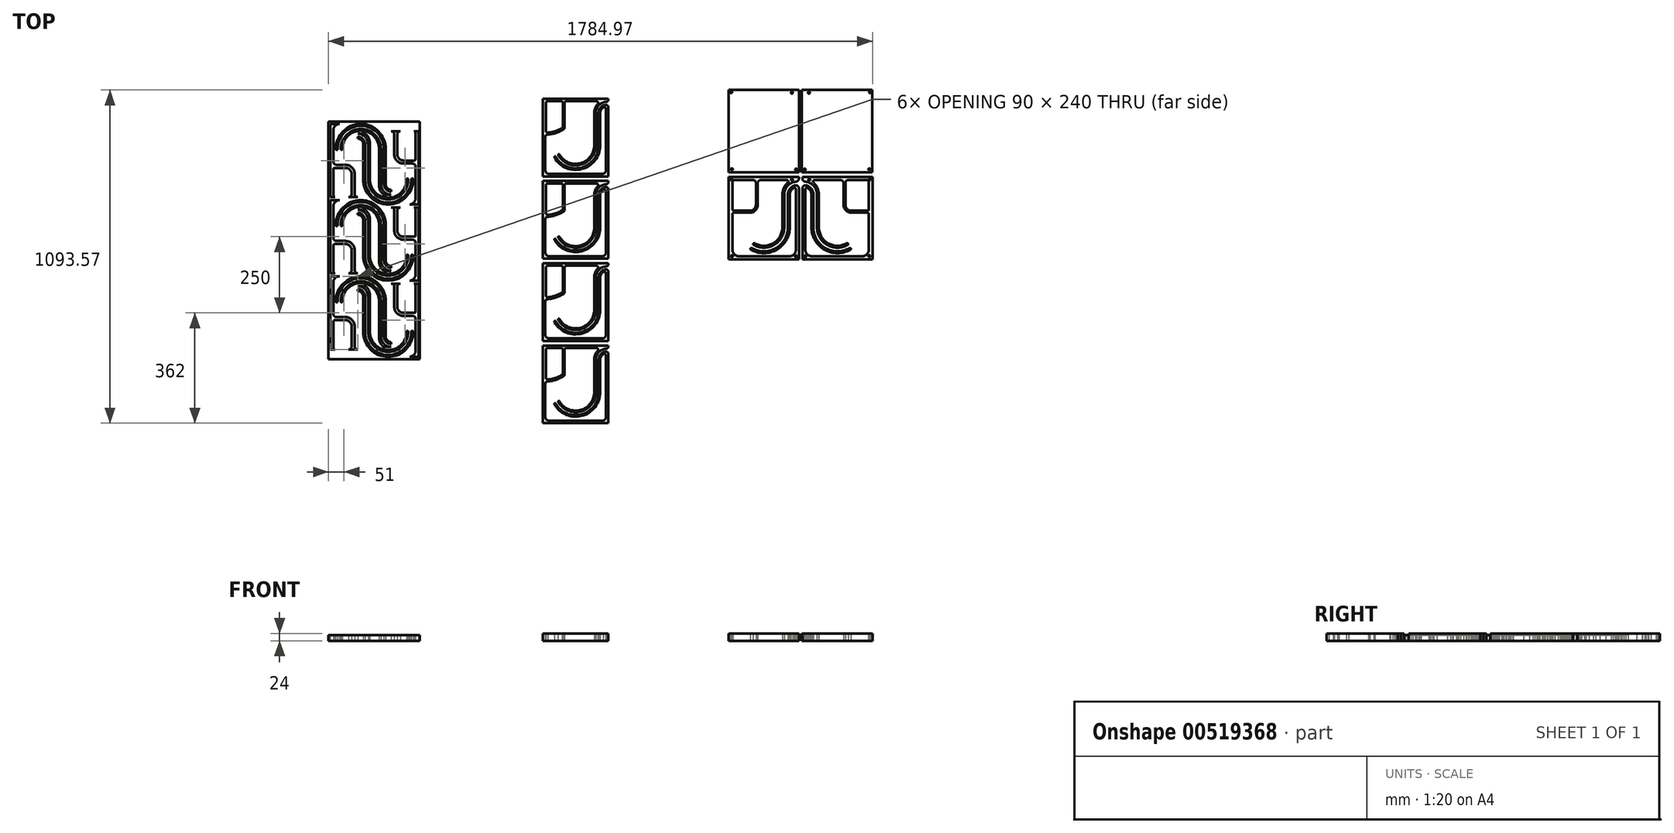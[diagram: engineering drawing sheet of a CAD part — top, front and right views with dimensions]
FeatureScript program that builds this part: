
annotation { "Feature Type Name" : "Feature", "Feature Type Description" : "" }
export const myFeature = defineFeature(function(context is Context, id is Id, definition is map)
    precondition{}
    {
        {
            var Q0;
            Q0=qCreatedBy(makeId("Top.planeOp"),FACE);
            var sketch = newSketch(context, id + "F0", { "sketchPlane" : qUnion([Q0])});
            skLineSegment(sketch, "E0", {"start": v(-576, 116) * mm, "end": v(-576, 0) * mm});
            skArc(sketch, "E1", {"start": v(-560, 116) * mm, "mid": v(-563.31, 134.85) * mm, "end": v(-575, 150) * mm});
            skArc(sketch, "E2", {"start": v(-582, 116) * mm, "mid": v(-587.27, 128.73) * mm, "end": v(-600, 134) * mm});
            skLineSegment(sketch, "E3", {"start": v(-600, 134) * mm, "end": v(-600, 140) * mm});
            skArc(sketch, "E4", {"start": v(-576, 116) * mm, "mid": v(-583.03, 132.97) * mm, "end": v(-600, 140) * mm});
            skArc(sketch, "E5", {"start": v(-566, 116) * mm, "mid": v(-575.96, 140.04) * mm, "end": v(-600, 150) * mm});
            skLineSegment(sketch, "E6", {"start": v(-582, 116) * mm, "end": v(-582, 0) * mm});
            skArc(sketch, "E7", {"start": v(-560, 0) * mm, "mid": v(-500, -60) * mm, "end": v(-440, 0) * mm});
            skLineSegment(sketch, "E8", {"start": v(-560, 116) * mm, "end": v(-560, 0) * mm});
            skArc(sketch, "E9", {"start": v(-566, 0) * mm, "mid": v(-500, -66) * mm, "end": v(-434, 0) * mm});
            skArc(sketch, "E10", {"start": v(-576, 0) * mm, "mid": v(-500, -76) * mm, "end": v(-424, 0) * mm});
            skArc(sketch, "E11", {"start": v(-582, 0) * mm, "mid": v(-500, -82) * mm, "end": v(-418, 0) * mm});
            skArc(sketch, "E12", {"start": v(-434, 0) * mm, "mid": v(-437, 3) * mm, "end": v(-440, 0) * mm});
            skArc(sketch, "E13", {"start": v(-418, 0) * mm, "mid": v(-421, 3) * mm, "end": v(-424, 0) * mm});
            skLineSegment(sketch, "E14", {"start": v(-600, 150) * mm, "end": v(-575, 150) * mm});
            skLineSegment(sketch, "E15", {"start": v(-566, 116) * mm, "end": v(-566, 0) * mm});
            skLineSegment(sketch, "E16", {"start": v(-514, -16) * mm, "end": v(-514, 100) * mm});
            skArc(sketch, "E17", {"start": v(-530, -16) * mm, "mid": v(-526.69, -34.85) * mm, "end": v(-515, -50) * mm});
            skArc(sketch, "E18", {"start": v(-508, -16) * mm, "mid": v(-502.73, -28.73) * mm, "end": v(-490, -34) * mm});
            skLineSegment(sketch, "E19", {"start": v(-490, -34) * mm, "end": v(-490, -40) * mm});
            skArc(sketch, "E20", {"start": v(-514, -16) * mm, "mid": v(-506.97, -32.97) * mm, "end": v(-490, -40) * mm});
            skArc(sketch, "E21", {"start": v(-524, -16) * mm, "mid": v(-514.04, -40.04) * mm, "end": v(-490, -50) * mm});
            skLineSegment(sketch, "E22", {"start": v(-508, -16) * mm, "end": v(-508, 100) * mm});
            skArc(sketch, "E23", {"start": v(-530, 100) * mm, "mid": v(-590, 160) * mm, "end": v(-650, 100) * mm});
            skLineSegment(sketch, "E24", {"start": v(-530, -16) * mm, "end": v(-530, 100) * mm});
            skArc(sketch, "E25", {"start": v(-524, 100) * mm, "mid": v(-590, 166) * mm, "end": v(-656, 100) * mm});
            skArc(sketch, "E26", {"start": v(-514, 100) * mm, "mid": v(-590, 176) * mm, "end": v(-666, 100) * mm});
            skArc(sketch, "E27", {"start": v(-508, 100) * mm, "mid": v(-590, 182) * mm, "end": v(-672, 100) * mm});
            skArc(sketch, "E28", {"start": v(-656, 100) * mm, "mid": v(-653, 97) * mm, "end": v(-650, 100) * mm});
            skArc(sketch, "E29", {"start": v(-672, 100) * mm, "mid": v(-669, 97) * mm, "end": v(-666, 100) * mm});
            skLineSegment(sketch, "E30", {"start": v(-490, -50) * mm, "end": v(-515, -50) * mm});
            skLineSegment(sketch, "E31", {"start": v(-524, -16) * mm, "end": v(-524, 100) * mm});
            skArc(sketch, "E32", {"start": v(-430, -82) * mm, "mid": v(-415.86, -76.14) * mm, "end": v(-410, -62) * mm});
            skArc(sketch, "E33", {"start": v(-410, 42) * mm, "mid": v(-412.93, 49.07) * mm, "end": v(-420, 52) * mm});
            skArc(sketch, "E34", {"start": v(-480, 148) * mm, "mid": v(-482.93, 155.07) * mm, "end": v(-490, 158) * mm});
            skArc(sketch, "E35", {"start": v(-460, 158) * mm, "mid": v(-467.07, 155.07) * mm, "end": v(-470, 148) * mm});
            skArc(sketch, "E36", {"start": v(-470, 82) * mm, "mid": v(-464.14, 67.86) * mm, "end": v(-450, 62) * mm});
            skArc(sketch, "E37", {"start": v(-480, 82) * mm, "mid": v(-471.21, 60.79) * mm, "end": v(-450, 52) * mm});
            skLineSegment(sketch, "E38", {"start": v(-480, 148) * mm, "end": v(-480, 82) * mm});
            skArc(sketch, "E39", {"start": v(-415, 62) * mm, "mid": v(-411.46, 63.46) * mm, "end": v(-410, 67) * mm});
            skArc(sketch, "E40", {"start": v(-410, 153) * mm, "mid": v(-411.46, 156.54) * mm, "end": v(-415, 158) * mm});
            skLineSegment(sketch, "E41", {"start": v(-410, 153) * mm, "end": v(-410, 67) * mm});
            skLineSegment(sketch, "E42", {"start": v(-400, -82) * mm, "end": v(-400, 158) * mm});
            skLineSegment(sketch, "E43", {"start": v(-400, 158) * mm, "end": v(-415, 158) * mm});
            skLineSegment(sketch, "E44", {"start": v(-430, -82) * mm, "end": v(-400, -82) * mm});
            skLineSegment(sketch, "E45", {"start": v(-410, 42) * mm, "end": v(-410, -62) * mm});
            skLineSegment(sketch, "E46", {"start": v(-420, 52) * mm, "end": v(-450, 52) * mm});
            skLineSegment(sketch, "E47", {"start": v(-415, 62) * mm, "end": v(-450, 62) * mm});
            skLineSegment(sketch, "E48", {"start": v(-490, 158) * mm, "end": v(-460, 158) * mm});
            skLineSegment(sketch, "E49", {"start": v(-470, 148) * mm, "end": v(-470, 82) * mm});
            skArc(sketch, "E50", {"start": v(-660, 182) * mm, "mid": v(-674.14, 176.14) * mm, "end": v(-680, 162) * mm});
            skArc(sketch, "E51", {"start": v(-680, 58) * mm, "mid": v(-677.07, 50.93) * mm, "end": v(-670, 48) * mm});
            skArc(sketch, "E52", {"start": v(-610, -48) * mm, "mid": v(-607.07, -55.07) * mm, "end": v(-600, -58) * mm});
            skArc(sketch, "E53", {"start": v(-630, -58) * mm, "mid": v(-622.93, -55.07) * mm, "end": v(-620, -48) * mm});
            skArc(sketch, "E54", {"start": v(-620, 18) * mm, "mid": v(-625.86, 32.14) * mm, "end": v(-640, 38) * mm});
            skArc(sketch, "E55", {"start": v(-610, 18) * mm, "mid": v(-618.79, 39.21) * mm, "end": v(-640, 48) * mm});
            skLineSegment(sketch, "E56", {"start": v(-610, -48) * mm, "end": v(-610, 18) * mm});
            skArc(sketch, "E57", {"start": v(-675, 38) * mm, "mid": v(-678.54, 36.54) * mm, "end": v(-680, 33) * mm});
            skArc(sketch, "E58", {"start": v(-680, -53) * mm, "mid": v(-678.54, -56.54) * mm, "end": v(-675, -58) * mm});
            skLineSegment(sketch, "E59", {"start": v(-680, -53) * mm, "end": v(-680, 33) * mm});
            skLineSegment(sketch, "E60", {"start": v(-690, 182) * mm, "end": v(-690, -58) * mm});
            skLineSegment(sketch, "E61", {"start": v(-690, -58) * mm, "end": v(-675, -58) * mm});
            skLineSegment(sketch, "E62", {"start": v(-660, 182) * mm, "end": v(-690, 182) * mm});
            skLineSegment(sketch, "E63", {"start": v(-680, 58) * mm, "end": v(-680, 162) * mm});
            skLineSegment(sketch, "E64", {"start": v(-670, 48) * mm, "end": v(-640, 48) * mm});
            skLineSegment(sketch, "E65", {"start": v(-675, 38) * mm, "end": v(-640, 38) * mm});
            skLineSegment(sketch, "E66", {"start": v(-600, -58) * mm, "end": v(-630, -58) * mm});
            skLineSegment(sketch, "E67", {"start": v(-620, -48) * mm, "end": v(-620, 18) * mm});
            skLineSegment(sketch, "E68", {"start": v(-576, 366) * mm, "end": v(-576, 250) * mm});
            skArc(sketch, "E69", {"start": v(-560, 366) * mm, "mid": v(-563.31, 384.85) * mm, "end": v(-575, 400) * mm});
            skArc(sketch, "E70", {"start": v(-582, 366) * mm, "mid": v(-587.27, 378.73) * mm, "end": v(-600, 384) * mm});
            skLineSegment(sketch, "E71", {"start": v(-600, 384) * mm, "end": v(-600, 390) * mm});
            skArc(sketch, "E72", {"start": v(-576, 366) * mm, "mid": v(-583.03, 382.97) * mm, "end": v(-600, 390) * mm});
            skArc(sketch, "E73", {"start": v(-566, 366) * mm, "mid": v(-575.96, 390.04) * mm, "end": v(-600, 400) * mm});
            skLineSegment(sketch, "E74", {"start": v(-582, 366) * mm, "end": v(-582, 250) * mm});
            skArc(sketch, "E75", {"start": v(-560, 250) * mm, "mid": v(-500, 190) * mm, "end": v(-440, 250) * mm});
            skLineSegment(sketch, "E76", {"start": v(-560, 366) * mm, "end": v(-560, 250) * mm});
            skArc(sketch, "E77", {"start": v(-566, 250) * mm, "mid": v(-500, 184) * mm, "end": v(-434, 250) * mm});
            skArc(sketch, "E78", {"start": v(-576, 250) * mm, "mid": v(-500, 174) * mm, "end": v(-424, 250) * mm});
            skArc(sketch, "E79", {"start": v(-582, 250) * mm, "mid": v(-500, 168) * mm, "end": v(-418, 250) * mm});
            skArc(sketch, "E80", {"start": v(-434, 250) * mm, "mid": v(-437, 253) * mm, "end": v(-440, 250) * mm});
            skArc(sketch, "E81", {"start": v(-418, 250) * mm, "mid": v(-421, 253) * mm, "end": v(-424, 250) * mm});
            skLineSegment(sketch, "E82", {"start": v(-600, 400) * mm, "end": v(-575, 400) * mm});
            skLineSegment(sketch, "E83", {"start": v(-566, 366) * mm, "end": v(-566, 250) * mm});
            skLineSegment(sketch, "E84", {"start": v(-514, 234) * mm, "end": v(-514, 350) * mm});
            skArc(sketch, "E85", {"start": v(-530, 234) * mm, "mid": v(-526.69, 215.15) * mm, "end": v(-515, 200) * mm});
            skArc(sketch, "E86", {"start": v(-508, 234) * mm, "mid": v(-502.73, 221.27) * mm, "end": v(-490, 216) * mm});
            skLineSegment(sketch, "E87", {"start": v(-490, 216) * mm, "end": v(-490, 210) * mm});
            skArc(sketch, "E88", {"start": v(-514, 234) * mm, "mid": v(-506.97, 217.03) * mm, "end": v(-490, 210) * mm});
            skArc(sketch, "E89", {"start": v(-524, 234) * mm, "mid": v(-514.04, 209.96) * mm, "end": v(-490, 200) * mm});
            skLineSegment(sketch, "E90", {"start": v(-508, 234) * mm, "end": v(-508, 350) * mm});
            skArc(sketch, "E91", {"start": v(-530, 350) * mm, "mid": v(-590, 410) * mm, "end": v(-650, 350) * mm});
            skLineSegment(sketch, "E92", {"start": v(-530, 234) * mm, "end": v(-530, 350) * mm});
            skArc(sketch, "E93", {"start": v(-524, 350) * mm, "mid": v(-590, 416) * mm, "end": v(-656, 350) * mm});
            skArc(sketch, "E94", {"start": v(-514, 350) * mm, "mid": v(-590, 426) * mm, "end": v(-666, 350) * mm});
            skArc(sketch, "E95", {"start": v(-508, 350) * mm, "mid": v(-590, 432) * mm, "end": v(-672, 350) * mm});
            skArc(sketch, "E96", {"start": v(-656, 350) * mm, "mid": v(-653, 347) * mm, "end": v(-650, 350) * mm});
            skArc(sketch, "E97", {"start": v(-672, 350) * mm, "mid": v(-669, 347) * mm, "end": v(-666, 350) * mm});
            skLineSegment(sketch, "E98", {"start": v(-490, 200) * mm, "end": v(-515, 200) * mm});
            skLineSegment(sketch, "E99", {"start": v(-524, 234) * mm, "end": v(-524, 350) * mm});
            skArc(sketch, "E100", {"start": v(-430, 168) * mm, "mid": v(-415.86, 173.86) * mm, "end": v(-410, 188) * mm});
            skArc(sketch, "E101", {"start": v(-410, 292) * mm, "mid": v(-412.93, 299.07) * mm, "end": v(-420, 302) * mm});
            skArc(sketch, "E102", {"start": v(-480, 398) * mm, "mid": v(-482.93, 405.07) * mm, "end": v(-490, 408) * mm});
            skArc(sketch, "E103", {"start": v(-460, 408) * mm, "mid": v(-467.07, 405.07) * mm, "end": v(-470, 398) * mm});
            skArc(sketch, "E104", {"start": v(-470, 332) * mm, "mid": v(-464.14, 317.86) * mm, "end": v(-450, 312) * mm});
            skArc(sketch, "E105", {"start": v(-480, 332) * mm, "mid": v(-471.21, 310.79) * mm, "end": v(-450, 302) * mm});
            skLineSegment(sketch, "E106", {"start": v(-480, 398) * mm, "end": v(-480, 332) * mm});
            skArc(sketch, "E107", {"start": v(-415, 312) * mm, "mid": v(-411.46, 313.46) * mm, "end": v(-410, 317) * mm});
            skArc(sketch, "E108", {"start": v(-410, 403) * mm, "mid": v(-411.46, 406.54) * mm, "end": v(-415, 408) * mm});
            skLineSegment(sketch, "E109", {"start": v(-410, 403) * mm, "end": v(-410, 317) * mm});
            skLineSegment(sketch, "E110", {"start": v(-400, 168) * mm, "end": v(-400, 408) * mm});
            skLineSegment(sketch, "E111", {"start": v(-400, 408) * mm, "end": v(-415, 408) * mm});
            skLineSegment(sketch, "E112", {"start": v(-430, 168) * mm, "end": v(-400, 168) * mm});
            skLineSegment(sketch, "E113", {"start": v(-410, 292) * mm, "end": v(-410, 188) * mm});
            skLineSegment(sketch, "E114", {"start": v(-420, 302) * mm, "end": v(-450, 302) * mm});
            skLineSegment(sketch, "E115", {"start": v(-415, 312) * mm, "end": v(-450, 312) * mm});
            skLineSegment(sketch, "E116", {"start": v(-490, 408) * mm, "end": v(-460, 408) * mm});
            skLineSegment(sketch, "E117", {"start": v(-470, 398) * mm, "end": v(-470, 332) * mm});
            skArc(sketch, "E118", {"start": v(-660, 432) * mm, "mid": v(-674.14, 426.14) * mm, "end": v(-680, 412) * mm});
            skArc(sketch, "E119", {"start": v(-680, 308) * mm, "mid": v(-677.07, 300.93) * mm, "end": v(-670, 298) * mm});
            skArc(sketch, "E120", {"start": v(-610, 202) * mm, "mid": v(-607.07, 194.93) * mm, "end": v(-600, 192) * mm});
            skArc(sketch, "E121", {"start": v(-630, 192) * mm, "mid": v(-622.93, 194.93) * mm, "end": v(-620, 202) * mm});
            skArc(sketch, "E122", {"start": v(-620, 268) * mm, "mid": v(-625.86, 282.14) * mm, "end": v(-640, 288) * mm});
            skArc(sketch, "E123", {"start": v(-610, 268) * mm, "mid": v(-618.79, 289.21) * mm, "end": v(-640, 298) * mm});
            skLineSegment(sketch, "E124", {"start": v(-610, 202) * mm, "end": v(-610, 268) * mm});
            skArc(sketch, "E125", {"start": v(-675, 288) * mm, "mid": v(-678.54, 286.54) * mm, "end": v(-680, 283) * mm});
            skArc(sketch, "E126", {"start": v(-680, 197) * mm, "mid": v(-678.54, 193.46) * mm, "end": v(-675, 192) * mm});
            skLineSegment(sketch, "E127", {"start": v(-680, 197) * mm, "end": v(-680, 283) * mm});
            skLineSegment(sketch, "E128", {"start": v(-690, 432) * mm, "end": v(-690, 192) * mm});
            skLineSegment(sketch, "E129", {"start": v(-690, 192) * mm, "end": v(-675, 192) * mm});
            skLineSegment(sketch, "E130", {"start": v(-660, 432) * mm, "end": v(-690, 432) * mm});
            skLineSegment(sketch, "E131", {"start": v(-680, 308) * mm, "end": v(-680, 412) * mm});
            skLineSegment(sketch, "E132", {"start": v(-670, 298) * mm, "end": v(-640, 298) * mm});
            skLineSegment(sketch, "E133", {"start": v(-675, 288) * mm, "end": v(-640, 288) * mm});
            skLineSegment(sketch, "E134", {"start": v(-600, 192) * mm, "end": v(-630, 192) * mm});
            skLineSegment(sketch, "E135", {"start": v(-620, 202) * mm, "end": v(-620, 268) * mm});
            skLineSegment(sketch, "E136", {"start": v(-576, -134) * mm, "end": v(-576, -250) * mm});
            skArc(sketch, "E137", {"start": v(-560, -134) * mm, "mid": v(-563.31, -115.15) * mm, "end": v(-575, -100) * mm});
            skArc(sketch, "E138", {"start": v(-582, -134) * mm, "mid": v(-587.27, -121.27) * mm, "end": v(-600, -116) * mm});
            skLineSegment(sketch, "E139", {"start": v(-600, -116) * mm, "end": v(-600, -110) * mm});
            skArc(sketch, "E140", {"start": v(-576, -134) * mm, "mid": v(-583.03, -117.03) * mm, "end": v(-600, -110) * mm});
            skArc(sketch, "E141", {"start": v(-566, -134) * mm, "mid": v(-575.96, -109.96) * mm, "end": v(-600, -100) * mm});
            skLineSegment(sketch, "E142", {"start": v(-582, -134) * mm, "end": v(-582, -250) * mm});
            skArc(sketch, "E143", {"start": v(-560, -250) * mm, "mid": v(-500, -310) * mm, "end": v(-440, -250) * mm});
            skLineSegment(sketch, "E144", {"start": v(-560, -134) * mm, "end": v(-560, -250) * mm});
            skArc(sketch, "E145", {"start": v(-566, -250) * mm, "mid": v(-500, -316) * mm, "end": v(-434, -250) * mm});
            skArc(sketch, "E146", {"start": v(-576, -250) * mm, "mid": v(-500, -326) * mm, "end": v(-424, -250) * mm});
            skArc(sketch, "E147", {"start": v(-582, -250) * mm, "mid": v(-500, -332) * mm, "end": v(-418, -250) * mm});
            skArc(sketch, "E148", {"start": v(-434, -250) * mm, "mid": v(-437, -247) * mm, "end": v(-440, -250) * mm});
            skArc(sketch, "E149", {"start": v(-418, -250) * mm, "mid": v(-421, -247) * mm, "end": v(-424, -250) * mm});
            skLineSegment(sketch, "E150", {"start": v(-600, -100) * mm, "end": v(-575, -100) * mm});
            skLineSegment(sketch, "E151", {"start": v(-566, -134) * mm, "end": v(-566, -250) * mm});
            skLineSegment(sketch, "E152", {"start": v(-514, -266) * mm, "end": v(-514, -150) * mm});
            skArc(sketch, "E153", {"start": v(-530, -266) * mm, "mid": v(-526.69, -284.85) * mm, "end": v(-515, -300) * mm});
            skArc(sketch, "E154", {"start": v(-508, -266) * mm, "mid": v(-502.73, -278.73) * mm, "end": v(-490, -284) * mm});
            skLineSegment(sketch, "E155", {"start": v(-490, -284) * mm, "end": v(-490, -290) * mm});
            skArc(sketch, "E156", {"start": v(-514, -266) * mm, "mid": v(-506.97, -282.97) * mm, "end": v(-490, -290) * mm});
            skArc(sketch, "E157", {"start": v(-524, -266) * mm, "mid": v(-514.04, -290.04) * mm, "end": v(-490, -300) * mm});
            skLineSegment(sketch, "E158", {"start": v(-508, -266) * mm, "end": v(-508, -150) * mm});
            skArc(sketch, "E159", {"start": v(-530, -150) * mm, "mid": v(-590, -90) * mm, "end": v(-650, -150) * mm});
            skLineSegment(sketch, "E160", {"start": v(-530, -266) * mm, "end": v(-530, -150) * mm});
            skArc(sketch, "E161", {"start": v(-524, -150) * mm, "mid": v(-590, -84) * mm, "end": v(-656, -150) * mm});
            skArc(sketch, "E162", {"start": v(-514, -150) * mm, "mid": v(-590, -74) * mm, "end": v(-666, -150) * mm});
            skArc(sketch, "E163", {"start": v(-508, -150) * mm, "mid": v(-590, -68) * mm, "end": v(-672, -150) * mm});
            skArc(sketch, "E164", {"start": v(-656, -150) * mm, "mid": v(-653, -153) * mm, "end": v(-650, -150) * mm});
            skArc(sketch, "E165", {"start": v(-672, -150) * mm, "mid": v(-669, -153) * mm, "end": v(-666, -150) * mm});
            skLineSegment(sketch, "E166", {"start": v(-490, -300) * mm, "end": v(-515, -300) * mm});
            skLineSegment(sketch, "E167", {"start": v(-524, -266) * mm, "end": v(-524, -150) * mm});
            skArc(sketch, "E168", {"start": v(-430, -332) * mm, "mid": v(-415.86, -326.14) * mm, "end": v(-410, -312) * mm});
            skArc(sketch, "E169", {"start": v(-410, -208) * mm, "mid": v(-412.93, -200.93) * mm, "end": v(-420, -198) * mm});
            skArc(sketch, "E170", {"start": v(-480, -102) * mm, "mid": v(-482.93, -94.93) * mm, "end": v(-490, -92) * mm});
            skArc(sketch, "E171", {"start": v(-460, -92) * mm, "mid": v(-467.07, -94.93) * mm, "end": v(-470, -102) * mm});
            skArc(sketch, "E172", {"start": v(-470, -168) * mm, "mid": v(-464.14, -182.14) * mm, "end": v(-450, -188) * mm});
            skArc(sketch, "E173", {"start": v(-480, -168) * mm, "mid": v(-471.21, -189.21) * mm, "end": v(-450, -198) * mm});
            skLineSegment(sketch, "E174", {"start": v(-480, -102) * mm, "end": v(-480, -168) * mm});
            skArc(sketch, "E175", {"start": v(-415, -188) * mm, "mid": v(-411.46, -186.54) * mm, "end": v(-410, -183) * mm});
            skArc(sketch, "E176", {"start": v(-410, -97) * mm, "mid": v(-411.46, -93.46) * mm, "end": v(-415, -92) * mm});
            skLineSegment(sketch, "E177", {"start": v(-410, -97) * mm, "end": v(-410, -183) * mm});
            skLineSegment(sketch, "E178", {"start": v(-400, -332) * mm, "end": v(-400, -92) * mm});
            skLineSegment(sketch, "E179", {"start": v(-400, -92) * mm, "end": v(-415, -92) * mm});
            skLineSegment(sketch, "E180", {"start": v(-430, -332) * mm, "end": v(-400, -332) * mm});
            skLineSegment(sketch, "E181", {"start": v(-410, -208) * mm, "end": v(-410, -312) * mm});
            skLineSegment(sketch, "E182", {"start": v(-420, -198) * mm, "end": v(-450, -198) * mm});
            skLineSegment(sketch, "E183", {"start": v(-415, -188) * mm, "end": v(-450, -188) * mm});
            skLineSegment(sketch, "E184", {"start": v(-490, -92) * mm, "end": v(-460, -92) * mm});
            skLineSegment(sketch, "E185", {"start": v(-470, -102) * mm, "end": v(-470, -168) * mm});
            skArc(sketch, "E186", {"start": v(-660, -68) * mm, "mid": v(-674.14, -73.86) * mm, "end": v(-680, -88) * mm});
            skArc(sketch, "E187", {"start": v(-680, -192) * mm, "mid": v(-677.07, -199.07) * mm, "end": v(-670, -202) * mm});
            skArc(sketch, "E188", {"start": v(-610, -298) * mm, "mid": v(-607.07, -305.07) * mm, "end": v(-600, -308) * mm});
            skArc(sketch, "E189", {"start": v(-630, -308) * mm, "mid": v(-622.93, -305.07) * mm, "end": v(-620, -298) * mm});
            skArc(sketch, "E190", {"start": v(-620, -232) * mm, "mid": v(-625.86, -217.86) * mm, "end": v(-640, -212) * mm});
            skArc(sketch, "E191", {"start": v(-610, -232) * mm, "mid": v(-618.79, -210.79) * mm, "end": v(-640, -202) * mm});
            skLineSegment(sketch, "E192", {"start": v(-610, -298) * mm, "end": v(-610, -232) * mm});
            skArc(sketch, "E193", {"start": v(-675, -212) * mm, "mid": v(-678.54, -213.46) * mm, "end": v(-680, -217) * mm});
            skArc(sketch, "E194", {"start": v(-680, -303) * mm, "mid": v(-678.54, -306.54) * mm, "end": v(-675, -308) * mm});
            skLineSegment(sketch, "E195", {"start": v(-680, -303) * mm, "end": v(-680, -217) * mm});
            skLineSegment(sketch, "E196", {"start": v(-690, -68) * mm, "end": v(-690, -308) * mm});
            skLineSegment(sketch, "E197", {"start": v(-690, -308) * mm, "end": v(-675, -308) * mm});
            skLineSegment(sketch, "E198", {"start": v(-660, -68) * mm, "end": v(-690, -68) * mm});
            skLineSegment(sketch, "E199", {"start": v(-680, -192) * mm, "end": v(-680, -88) * mm});
            skLineSegment(sketch, "E200", {"start": v(-670, -202) * mm, "end": v(-640, -202) * mm});
            skLineSegment(sketch, "E201", {"start": v(-675, -212) * mm, "end": v(-640, -212) * mm});
            skLineSegment(sketch, "E202", {"start": v(-600, -308) * mm, "end": v(-630, -308) * mm});
            skLineSegment(sketch, "E203", {"start": v(-620, -298) * mm, "end": v(-620, -232) * mm});
            skLineSegment(sketch, "E204.bottom", {"start": v(-696, 440) * mm, "end": v(-396, 440) * mm});
            skLineSegment(sketch, "E204.top", {"start": v(-696, -340) * mm, "end": v(-396, -340) * mm});
            skLineSegment(sketch, "E204.left", {"start": v(-696, 440) * mm, "end": v(-696, -340) * mm});
            skLineSegment(sketch, "E204.right", {"start": v(-396, 440) * mm, "end": v(-396, -340) * mm});
            skSolve(sketch);
        }
        {
            var Q0;
            Q0 = qSketchRegion(id + "F0", true);
            extrude(context, id + "F1", {"entities" : qUnion([Q0]), "depth" : 18 * mm, "offsetDistance" : 25 * mm});
        }
        {
            var Q0;
            Q0=qCreatedBy(makeId("Top.planeOp"),FACE);
            var sketch = newSketch(context, id + "F2", { "sketchPlane" : qUnion([Q0])});
            skArc(sketch, "E205.MirrorCS", {"start": v(649.59, -1.9) * mm, "mid": v(635.45, 3.96) * mm, "end": v(629.59, 18.1) * mm});
            skArc(sketch, "E206.MirrorCS", {"start": v(634.59, 147.1) * mm, "mid": v(631.05, 148.57) * mm, "end": v(629.59, 152.1) * mm});
            skLineSegment(sketch, "E207", {"start": v(629.59, 152.1) * mm, "end": v(629.59, 243.1) * mm});
            skArc(sketch, "E208", {"start": v(634.59, 248.1) * mm, "mid": v(631.05, 246.64) * mm, "end": v(629.59, 243.1) * mm});
            skLineSegment(sketch, "E209", {"start": v(634.59, 248.1) * mm, "end": v(696.59, 248.1) * mm});
            skArc(sketch, "E210", {"start": v(706.59, 238.1) * mm, "mid": v(703.66, 245.18) * mm, "end": v(696.59, 248.1) * mm});
            skLineSegment(sketch, "E211", {"start": v(706.59, 238.1) * mm, "end": v(706.59, 167.1) * mm});
            skArc(sketch, "E212", {"start": v(686.59, 147.1) * mm, "mid": v(700.73, 152.96) * mm, "end": v(706.59, 167.1) * mm});
            skArc(sketch, "E213", {"start": v(793.59, 93.1) * mm, "mid": v(763.09, 40.28) * mm, "end": v(702.09, 40.28) * mm});
            skLineSegment(sketch, "E214.bottom", {"start": v(617.59, -11.9) * mm, "end": v(847.59, -11.9) * mm});
            skLineSegment(sketch, "E214.top", {"start": v(617.59, 258.1) * mm, "end": v(847.59, 258.1) * mm});
            skLineSegment(sketch, "E214.left", {"start": v(617.59, -11.9) * mm, "end": v(617.59, 258.1) * mm});
            skArc(sketch, "E215", {"start": v(817.59, 93.1) * mm, "mid": v(775.09, 19.5) * mm, "end": v(690.09, 19.5) * mm});
            skLineSegment(sketch, "E216", {"start": v(686.59, 147.1) * mm, "end": v(634.59, 147.1) * mm});
            skLineSegment(sketch, "E217", {"start": v(634.59, 141.1) * mm, "end": v(686.59, 141.1) * mm});
            skLineSegment(sketch, "E218", {"start": v(712.59, 238.1) * mm, "end": v(712.59, 167.1) * mm});
            skArc(sketch, "E219", {"start": v(686.59, 141.1) * mm, "mid": v(704.97, 148.72) * mm, "end": v(712.59, 167.1) * mm});
            skArc(sketch, "E220", {"start": v(722.59, 248.1) * mm, "mid": v(715.52, 245.18) * mm, "end": v(712.59, 238.1) * mm});
            skArc(sketch, "E221", {"start": v(634.59, 141.1) * mm, "mid": v(631.05, 139.64) * mm, "end": v(629.59, 136.1) * mm});
            skLineSegment(sketch, "E222", {"start": v(629.59, 136.1) * mm, "end": v(629.59, 18.1) * mm});
            skLineSegment(sketch, "E223", {"start": v(649.59, -1.9) * mm, "end": v(817.59, -1.9) * mm});
            skArc(sketch, "E224", {"start": v(817.59, -1.9) * mm, "mid": v(831.73, 3.96) * mm, "end": v(837.59, 18.1) * mm});
            skLineSegment(sketch, "E225", {"start": v(847.59, 258.1) * mm, "end": v(847.59, 253.1) * mm});
            skLineSegment(sketch, "E226", {"start": v(847.59, -11.9) * mm, "end": v(847.59, 221.1) * mm});
            skLineSegment(sketch, "E227", {"start": v(817.59, 93.1) * mm, "end": v(817.59, 200.1) * mm});
            skLineSegment(sketch, "E228", {"start": v(793.59, 93.1) * mm, "end": v(793.59, 200.1) * mm});
            skArc(sketch, "E229", {"start": v(817.59, 200.1) * mm, "mid": v(821.09, 212.87) * mm, "end": v(830.61, 222.05) * mm});
            skLineSegment(sketch, "E230", {"start": v(837.59, 18.1) * mm, "end": v(837.59, 217.6) * mm});
            skArc(sketch, "E231", {"start": v(837.59, 217.6) * mm, "mid": v(835.28, 221.68) * mm, "end": v(830.61, 222.05) * mm});
            skLineSegment(sketch, "E232", {"start": v(722.59, 248.1) * mm, "end": v(807.59, 248.1) * mm});
            skArc(sketch, "E233", {"start": v(811.82, 240.44) * mm, "mid": v(811.97, 245.52) * mm, "end": v(807.59, 248.1) * mm});
            skArc(sketch, "E234", {"start": v(811.82, 240.44) * mm, "mid": v(798.47, 222.19) * mm, "end": v(793.59, 200.1) * mm});
            skArc(sketch, "E235", {"start": v(799.59, 93.1) * mm, "mid": v(766.09, 35.08) * mm, "end": v(699.09, 35.08) * mm});
            skArc(sketch, "E236", {"start": v(811.59, 93.1) * mm, "mid": v(772.09, 24.7) * mm, "end": v(693.09, 24.7) * mm});
            skLineSegment(sketch, "E237", {"start": v(799.59, 200.1) * mm, "end": v(799.59, 93.1) * mm});
            skLineSegment(sketch, "E238", {"start": v(811.59, 200.1) * mm, "end": v(811.59, 93.1) * mm});
            skArc(sketch, "E239", {"start": v(702.09, 40.28) * mm, "mid": v(697.99, 39.18) * mm, "end": v(699.09, 35.08) * mm});
            skArc(sketch, "E240", {"start": v(693.09, 24.7) * mm, "mid": v(688.99, 23.6) * mm, "end": v(690.09, 19.5) * mm});
            skArc(sketch, "E241", {"start": v(811.59, 200.1) * mm, "mid": v(818.39, 219.48) * mm, "end": v(835.8, 230.35) * mm});
            skArc(sketch, "E242", {"start": v(847.59, 221.1) * mm, "mid": v(843.78, 228.39) * mm, "end": v(835.8, 230.35) * mm});
            skArc(sketch, "E243", {"start": v(799.59, 200.1) * mm, "mid": v(810.46, 228.69) * mm, "end": v(837.59, 242.81) * mm});
            skArc(sketch, "E244", {"start": v(837.59, 242.81) * mm, "mid": v(844.76, 245.85) * mm, "end": v(847.59, 253.1) * mm});
            skCircle(sketch, "E245", {"center": v(625.09, 250.6) * mm, "radius": 3 * mm});
            skCircle(sketch, "E246", {"center": v(627.59, -1.9) * mm, "radius": 3 * mm});
            skCircle(sketch, "E247", {"center": v(838.59, -2.9) * mm, "radius": 3 * mm});
            skCircle(sketch, "E248", {"center": v(824.59, 249.1) * mm, "radius": 3 * mm});
            skLineSegment(sketch, "E249.bottom", {"start": v(617.59, 273.57) * mm, "end": v(847.59, 273.57) * mm});
            skLineSegment(sketch, "E249.top", {"start": v(617.59, 543.57) * mm, "end": v(847.59, 543.57) * mm});
            skLineSegment(sketch, "E249.left", {"start": v(617.59, 273.57) * mm, "end": v(617.59, 543.57) * mm});
            skLineSegment(sketch, "E249.right", {"start": v(847.59, 273.57) * mm, "end": v(847.59, 543.57) * mm});
            skLineSegment(sketch, "E250.bottom", {"start": v(857.59, 273.57) * mm, "end": v(1088.59, 273.57) * mm});
            skLineSegment(sketch, "E250.top", {"start": v(857.59, 543.57) * mm, "end": v(1088.59, 543.57) * mm});
            skLineSegment(sketch, "E250.left", {"start": v(857.59, 273.57) * mm, "end": v(857.59, 543.57) * mm});
            skLineSegment(sketch, "E250.right", {"start": v(1088.59, 273.57) * mm, "end": v(1088.59, 543.57) * mm});
            skCircle(sketch, "E251", {"center": v(625.09, 536.07) * mm, "radius": 3 * mm});
            skCircle(sketch, "E252", {"center": v(1081.09, 536.07) * mm, "radius": 3 * mm});
            skCircle(sketch, "E253", {"center": v(824.59, 534.57) * mm, "radius": 3 * mm});
            skCircle(sketch, "E254", {"center": v(880.59, 534.57) * mm, "radius": 3 * mm});
            skCircle(sketch, "E255", {"center": v(627.59, 283.57) * mm, "radius": 3 * mm});
            skCircle(sketch, "E256", {"center": v(838.59, 282.57) * mm, "radius": 3 * mm});
            skCircle(sketch, "E257", {"center": v(866.59, 282.57) * mm, "radius": 3 * mm});
            skCircle(sketch, "E258", {"center": v(1078.59, 283.57) * mm, "radius": 3 * mm});
            skLineSegment(sketch, "E259", {"start": v(853.28, 261.8) * mm, "end": v(853.28, -18.2) * mm, "construction": true});
            skLineSegment(sketch, "E260.MirrorCS", {"start": v(1088.97, 258.1) * mm, "end": v(858.97, 258.1) * mm});
            skLineSegment(sketch, "E261.MirrorCS", {"start": v(858.97, 258.1) * mm, "end": v(858.97, 253.1) * mm});
            skArc(sketch, "E262.MirrorCS", {"start": v(868.97, 242.81) * mm, "mid": v(861.8, 245.85) * mm, "end": v(858.97, 253.1) * mm});
            skArc(sketch, "E263.MirrorCS", {"start": v(906.97, 200.1) * mm, "mid": v(896.1, 228.69) * mm, "end": v(868.97, 242.81) * mm});
            skArc(sketch, "E264.MirrorCS", {"start": v(894.75, 240.44) * mm, "mid": v(908.1, 222.19) * mm, "end": v(912.97, 200.1) * mm});
            skArc(sketch, "E265.MirrorCS", {"start": v(894.75, 240.44) * mm, "mid": v(894.6, 245.52) * mm, "end": v(898.97, 248.1) * mm});
            skLineSegment(sketch, "E266.MirrorCS", {"start": v(983.97, 248.1) * mm, "end": v(898.97, 248.1) * mm});
            skCircle(sketch, "E267.MirrorC", {"center": v(881.97, 249.1) * mm, "radius": 3 * mm});
            skArc(sketch, "E268.MirrorCS", {"start": v(894.97, 200.1) * mm, "mid": v(888.18, 219.48) * mm, "end": v(870.76, 230.35) * mm});
            skArc(sketch, "E269.MirrorCS", {"start": v(858.97, 221.1) * mm, "mid": v(862.78, 228.39) * mm, "end": v(870.76, 230.35) * mm});
            skLineSegment(sketch, "E270.MirrorCS", {"start": v(858.97, -11.9) * mm, "end": v(858.97, 221.1) * mm});
            skLineSegment(sketch, "E271.MirrorCS", {"start": v(868.97, 18.1) * mm, "end": v(868.97, 217.6) * mm});
            skArc(sketch, "E272.MirrorCS", {"start": v(868.97, 217.6) * mm, "mid": v(871.28, 221.68) * mm, "end": v(875.95, 222.05) * mm});
            skArc(sketch, "E273.MirrorCS", {"start": v(888.97, 200.1) * mm, "mid": v(885.47, 212.87) * mm, "end": v(875.95, 222.05) * mm});
            skLineSegment(sketch, "E274.MirrorCS", {"start": v(888.97, 93.1) * mm, "end": v(888.97, 200.1) * mm});
            skLineSegment(sketch, "E275.MirrorCS", {"start": v(894.97, 200.1) * mm, "end": v(894.97, 93.1) * mm});
            skLineSegment(sketch, "E276.MirrorCS", {"start": v(906.97, 200.1) * mm, "end": v(906.97, 93.1) * mm});
            skLineSegment(sketch, "E277.MirrorCS", {"start": v(912.97, 93.1) * mm, "end": v(912.97, 200.1) * mm});
            skArc(sketch, "E278.MirrorCS", {"start": v(888.97, -1.9) * mm, "mid": v(874.83, 3.96) * mm, "end": v(868.97, 18.1) * mm});
            skCircle(sketch, "E279.MirrorC", {"center": v(867.97, -2.9) * mm, "radius": 3 * mm});
            skLineSegment(sketch, "E280.MirrorCS", {"start": v(1088.97, -11.9) * mm, "end": v(858.97, -11.9) * mm});
            skArc(sketch, "E281.MirrorCS", {"start": v(888.97, 93.1) * mm, "mid": v(931.47, 19.5) * mm, "end": v(1016.47, 19.5) * mm});
            skArc(sketch, "E282.MirrorCS", {"start": v(894.97, 93.1) * mm, "mid": v(934.47, 24.7) * mm, "end": v(1013.47, 24.7) * mm});
            skArc(sketch, "E283.MirrorCS", {"start": v(906.97, 93.1) * mm, "mid": v(940.47, 35.08) * mm, "end": v(1007.47, 35.08) * mm});
            skArc(sketch, "E284.MirrorCS", {"start": v(912.97, 93.1) * mm, "mid": v(943.47, 40.28) * mm, "end": v(1004.47, 40.28) * mm});
            skArc(sketch, "E285.MirrorCS", {"start": v(1004.47, 40.28) * mm, "mid": v(1008.57, 39.18) * mm, "end": v(1007.47, 35.08) * mm});
            skArc(sketch, "E286.MirrorCS", {"start": v(1013.47, 24.7) * mm, "mid": v(1017.57, 23.6) * mm, "end": v(1016.47, 19.5) * mm});
            skArc(sketch, "E287.MirrorCS", {"start": v(1056.97, -1.9) * mm, "mid": v(1071.12, 3.96) * mm, "end": v(1076.97, 18.1) * mm});
            skLineSegment(sketch, "E288.MirrorCS", {"start": v(1056.97, -1.9) * mm, "end": v(888.97, -1.9) * mm});
            skCircle(sketch, "E289.MirrorC", {"center": v(1078.97, -1.9) * mm, "radius": 3 * mm});
            skLineSegment(sketch, "E290.MirrorCS", {"start": v(1088.97, -11.9) * mm, "end": v(1088.97, 258.1) * mm});
            skLineSegment(sketch, "E291.MirrorCS", {"start": v(1076.97, 136.1) * mm, "end": v(1076.97, 18.1) * mm});
            skArc(sketch, "E292.MirrorCS", {"start": v(1071.97, 141.1) * mm, "mid": v(1075.51, 139.64) * mm, "end": v(1076.97, 136.1) * mm});
            skArc(sketch, "E293.MirrorCS", {"start": v(1071.97, 147.1) * mm, "mid": v(1075.51, 148.57) * mm, "end": v(1076.97, 152.1) * mm});
            skLineSegment(sketch, "E294.MirrorCS", {"start": v(1019.97, 147.1) * mm, "end": v(1071.97, 147.1) * mm});
            skLineSegment(sketch, "E295.MirrorCS", {"start": v(1071.97, 141.1) * mm, "end": v(1019.97, 141.1) * mm});
            skLineSegment(sketch, "E296.MirrorCS", {"start": v(1076.97, 152.1) * mm, "end": v(1076.97, 243.1) * mm});
            skArc(sketch, "E297.MirrorCS", {"start": v(1019.97, 147.1) * mm, "mid": v(1005.83, 152.96) * mm, "end": v(999.97, 167.1) * mm});
            skArc(sketch, "E298.MirrorCS", {"start": v(1019.97, 141.1) * mm, "mid": v(1001.59, 148.72) * mm, "end": v(993.97, 167.1) * mm});
            skLineSegment(sketch, "E299.MirrorCS", {"start": v(993.97, 238.1) * mm, "end": v(993.97, 167.1) * mm});
            skLineSegment(sketch, "E300.MirrorCS", {"start": v(999.97, 238.1) * mm, "end": v(999.97, 167.1) * mm});
            skArc(sketch, "E301.MirrorCS", {"start": v(983.97, 248.1) * mm, "mid": v(991.05, 245.18) * mm, "end": v(993.97, 238.1) * mm});
            skArc(sketch, "E302.MirrorCS", {"start": v(999.97, 238.1) * mm, "mid": v(1002.9, 245.18) * mm, "end": v(1009.97, 248.1) * mm});
            skLineSegment(sketch, "E303.MirrorCS", {"start": v(1071.97, 248.1) * mm, "end": v(1009.97, 248.1) * mm});
            skArc(sketch, "E304.MirrorCS", {"start": v(1071.97, 248.1) * mm, "mid": v(1075.51, 246.64) * mm, "end": v(1076.97, 243.1) * mm});
            skCircle(sketch, "E305.MirrorC", {"center": v(1081.47, 250.6) * mm, "radius": 3 * mm});
            skSolve(sketch);
        }
        {
            var Q0;
            Q0 = qSketchRegion(id + "F2", true);
            extrude(context, id + "F3", {"entities" : qUnion([Q0]), "depth" : 24 * mm, "offsetDistance" : 25 * mm});
        }
        {
            var Q0;
            Q0=qCreatedBy(makeId("Top.planeOp"),FACE);
            var sketch = newSketch(context, id + "F4", { "sketchPlane" : qUnion([Q0])});
            skPoint(sketch, "E306.middle", {"position": v(0, 0) * mm});
            skArc(sketch, "E307.MirrorCS", {"start": v(28, -542) * mm, "mid": v(19.16, -538.34) * mm, "end": v(15.5, -529.5) * mm});
            skArc(sketch, "E308", {"start": v(187.98, -312.1) * mm, "mid": v(188.07, -306.05) * mm, "end": v(182.84, -303) * mm});
            skArc(sketch, "E309", {"start": v(176, -342) * mm, "mid": v(179, -325.85) * mm, "end": v(187.98, -312.1) * mm});
            skLineSegment(sketch, "E310", {"start": v(115, -448) * mm, "end": v(28.4, -498) * mm, "construction": true});
            skArc(sketch, "E311", {"start": v(181, -448) * mm, "mid": v(132.08, -511.75) * mm, "end": v(57.84, -481) * mm});
            skArc(sketch, "E312", {"start": v(176, -448) * mm, "mid": v(130.79, -506.92) * mm, "end": v(62.17, -478.5) * mm});
            skLineSegment(sketch, "E313", {"start": v(28, -542) * mm, "end": v(202.08, -542) * mm});
            skArc(sketch, "E314", {"start": v(202.08, -542) * mm, "mid": v(210.92, -538.34) * mm, "end": v(214.58, -529.5) * mm});
            skLineSegment(sketch, "E315.bottom", {"start": v(7.5, -550) * mm, "end": v(222.5, -550) * mm});
            skLineSegment(sketch, "E315.top", {"start": v(7.5, -295) * mm, "end": v(222.5, -295) * mm});
            skLineSegment(sketch, "E315.left", {"start": v(7.5, -550) * mm, "end": v(7.5, -295) * mm});
            skPoint(sketch, "E315.middle", {"position": v(115, -422.5) * mm});
            skArc(sketch, "E316", {"start": v(23.5, -412.7) * mm, "mid": v(17.84, -415.05) * mm, "end": v(15.5, -420.7) * mm});
            skArc(sketch, "E317", {"start": v(214.5, -305.62) * mm, "mid": v(220.16, -303.28) * mm, "end": v(222.5, -297.62) * mm});
            skLineSegment(sketch, "E318", {"start": v(222.5, -295) * mm, "end": v(222.5, -297.62) * mm});
            skLineSegment(sketch, "E319", {"start": v(222.5, -550) * mm, "end": v(222.5, -323.24) * mm});
            skArc(sketch, "E320", {"start": v(222.5, -323.24) * mm, "mid": v(219.78, -317.22) * mm, "end": v(213.46, -315.3) * mm});
            skArc(sketch, "E321", {"start": v(190.5, -448) * mm, "mid": v(134.54, -520.93) * mm, "end": v(49.62, -485.75) * mm});
            skArc(sketch, "E322", {"start": v(195.5, -448) * mm, "mid": v(135.83, -525.76) * mm, "end": v(45.28, -488.25) * mm});
            skArc(sketch, "E323", {"start": v(49.62, -485.75) * mm, "mid": v(46.2, -484.83) * mm, "end": v(45.28, -488.25) * mm});
            skArc(sketch, "E324", {"start": v(62.17, -478.5) * mm, "mid": v(58.76, -477.58) * mm, "end": v(57.84, -481) * mm});
            skLineSegment(sketch, "E325", {"start": v(15.5, -420.7) * mm, "end": v(15.5, -529.5) * mm});
            skArc(sketch, "E326", {"start": v(17.5, -400.7) * mm, "mid": v(19.26, -404.95) * mm, "end": v(23.5, -406.7) * mm});
            skArc(sketch, "E327", {"start": v(84.98, -303) * mm, "mid": v(80.74, -304.76) * mm, "end": v(78.98, -309) * mm});
            skArc(sketch, "E328", {"start": v(72.98, -309) * mm, "mid": v(71.22, -304.76) * mm, "end": v(66.98, -303) * mm});
            skArc(sketch, "E329", {"start": v(181, -342) * mm, "mid": v(190.65, -317.27) * mm, "end": v(214.5, -305.62) * mm});
            skLineSegment(sketch, "E330", {"start": v(181, -448) * mm, "end": v(181, -342) * mm});
            skArc(sketch, "E331", {"start": v(190.5, -342) * mm, "mid": v(197.03, -324.4) * mm, "end": v(213.46, -315.3) * mm});
            skLineSegment(sketch, "E332", {"start": v(176, -448) * mm, "end": v(176, -342) * mm});
            skLineSegment(sketch, "E333", {"start": v(66.98, -303) * mm, "end": v(23.5, -303) * mm});
            skArc(sketch, "E334", {"start": v(23.5, -303) * mm, "mid": v(19.26, -304.76) * mm, "end": v(17.5, -309) * mm});
            skLineSegment(sketch, "E335", {"start": v(17.5, -309) * mm, "end": v(17.5, -400.7) * mm});
            skLineSegment(sketch, "E336", {"start": v(84.98, -303) * mm, "end": v(182.84, -303) * mm});
            skArc(sketch, "E337", {"start": v(23.5, -412.7) * mm, "mid": v(51.54, -406.93) * mm, "end": v(77.13, -394.11) * mm});
            skLineSegment(sketch, "E338", {"start": v(190.5, -448) * mm, "end": v(190.5, -342) * mm});
            skLineSegment(sketch, "E339", {"start": v(195.5, -448) * mm, "end": v(195.5, -342) * mm});
            skLineSegment(sketch, "E340", {"start": v(78.98, -309) * mm, "end": v(78.98, -389) * mm});
            skArc(sketch, "E341", {"start": v(77.13, -394.11) * mm, "mid": v(78.5, -391.72) * mm, "end": v(78.98, -389) * mm});
            skLineSegment(sketch, "E342", {"start": v(72.98, -309) * mm, "end": v(72.98, -386.5) * mm});
            skArc(sketch, "E343", {"start": v(23.5, -406.7) * mm, "mid": v(48.17, -401.75) * mm, "end": v(70.92, -391.02) * mm});
            skArc(sketch, "E344", {"start": v(70.92, -391.02) * mm, "mid": v(72.44, -388.98) * mm, "end": v(72.98, -386.5) * mm});
            skArc(sketch, "E345", {"start": v(195.5, -342) * mm, "mid": v(197.99, -331.84) * mm, "end": v(204.88, -323.98) * mm});
            skArc(sketch, "E346", {"start": v(214.5, -328.76) * mm, "mid": v(211.17, -323.4) * mm, "end": v(204.88, -323.98) * mm});
            skLineSegment(sketch, "E347", {"start": v(214.5, -328.76) * mm, "end": v(214.58, -529.5) * mm});
            skLineSegment(sketch, "E348.0.1.0", {"start": v(7.5, -280) * mm, "end": v(7.5, -25) * mm});
            skLineSegment(sketch, "E348.0.1.1", {"start": v(7.5, -25) * mm, "end": v(222.5, -25) * mm});
            skArc(sketch, "E348.0.1.2", {"start": v(23.5, -33) * mm, "mid": v(19.26, -34.76) * mm, "end": v(17.5, -39) * mm});
            skLineSegment(sketch, "E348.0.1.3", {"start": v(66.98, -33) * mm, "end": v(23.5, -33) * mm});
            skLineSegment(sketch, "E348.0.1.4", {"start": v(17.5, -39) * mm, "end": v(17.5, -130.7) * mm});
            skLineSegment(sketch, "E348.0.1.5", {"start": v(72.98, -39) * mm, "end": v(72.98, -116.5) * mm});
            skLineSegment(sketch, "E348.0.1.6", {"start": v(78.98, -39) * mm, "end": v(78.98, -119) * mm});
            skArc(sketch, "E348.0.1.7", {"start": v(72.98, -39) * mm, "mid": v(71.22, -34.76) * mm, "end": v(66.98, -33) * mm});
            skArc(sketch, "E348.0.1.8", {"start": v(84.98, -33) * mm, "mid": v(80.74, -34.76) * mm, "end": v(78.98, -39) * mm});
            skLineSegment(sketch, "E348.0.1.9", {"start": v(84.98, -33) * mm, "end": v(182.84, -33) * mm});
            skArc(sketch, "E348.0.1.10", {"start": v(17.5, -130.7) * mm, "mid": v(19.26, -134.95) * mm, "end": v(23.5, -136.7) * mm});
            skArc(sketch, "E348.0.1.11", {"start": v(23.5, -142.7) * mm, "mid": v(17.84, -145.05) * mm, "end": v(15.5, -150.7) * mm});
            skArc(sketch, "E348.0.1.12", {"start": v(23.5, -136.7) * mm, "mid": v(48.17, -131.75) * mm, "end": v(70.92, -121.02) * mm});
            skArc(sketch, "E348.0.1.13", {"start": v(23.5, -142.7) * mm, "mid": v(51.54, -136.93) * mm, "end": v(77.13, -124.11) * mm});
            skArc(sketch, "E348.0.1.14", {"start": v(70.92, -121.02) * mm, "mid": v(72.44, -118.98) * mm, "end": v(72.98, -116.5) * mm});
            skArc(sketch, "E348.0.1.15", {"start": v(77.13, -124.11) * mm, "mid": v(78.5, -121.72) * mm, "end": v(78.98, -119) * mm});
            skLineSegment(sketch, "E348.0.1.16", {"start": v(15.5, -150.7) * mm, "end": v(15.5, -259.5) * mm});
            skArc(sketch, "E348.0.1.17", {"start": v(28, -272) * mm, "mid": v(19.16, -268.34) * mm, "end": v(15.5, -259.5) * mm});
            skLineSegment(sketch, "E348.0.1.18", {"start": v(7.5, -280) * mm, "end": v(222.5, -280) * mm});
            skLineSegment(sketch, "E348.0.1.19", {"start": v(28, -272) * mm, "end": v(202.08, -272) * mm});
            skArc(sketch, "E348.0.1.20", {"start": v(195.5, -178) * mm, "mid": v(135.83, -255.76) * mm, "end": v(45.28, -218.25) * mm});
            skArc(sketch, "E348.0.1.21", {"start": v(190.5, -178) * mm, "mid": v(134.54, -250.93) * mm, "end": v(49.62, -215.75) * mm});
            skArc(sketch, "E348.0.1.22", {"start": v(181, -178) * mm, "mid": v(132.08, -241.75) * mm, "end": v(57.84, -211) * mm});
            skArc(sketch, "E348.0.1.23", {"start": v(176, -178) * mm, "mid": v(130.79, -236.92) * mm, "end": v(62.17, -208.5) * mm});
            skArc(sketch, "E348.0.1.24", {"start": v(62.17, -208.5) * mm, "mid": v(58.76, -207.58) * mm, "end": v(57.84, -211) * mm});
            skArc(sketch, "E348.0.1.25", {"start": v(49.62, -215.75) * mm, "mid": v(46.2, -214.83) * mm, "end": v(45.28, -218.25) * mm});
            skLineSegment(sketch, "E348.0.1.26", {"start": v(115, -178) * mm, "end": v(28.4, -228) * mm, "construction": true});
            skPoint(sketch, "E348.0.1.27", {"position": v(115, -152.5) * mm});
            skLineSegment(sketch, "E348.0.1.28", {"start": v(176, -178) * mm, "end": v(176, -72) * mm});
            skLineSegment(sketch, "E348.0.1.29", {"start": v(181, -178) * mm, "end": v(181, -72) * mm});
            skLineSegment(sketch, "E348.0.1.30", {"start": v(190.5, -178) * mm, "end": v(190.5, -72) * mm});
            skLineSegment(sketch, "E348.0.1.31", {"start": v(195.5, -178) * mm, "end": v(195.5, -72) * mm});
            skArc(sketch, "E348.0.1.32", {"start": v(176, -72) * mm, "mid": v(179, -55.85) * mm, "end": v(187.98, -42.1) * mm});
            skArc(sketch, "E348.0.1.33", {"start": v(187.98, -42.1) * mm, "mid": v(188.07, -36.05) * mm, "end": v(182.84, -33) * mm});
            skArc(sketch, "E348.0.1.34", {"start": v(214.5, -35.62) * mm, "mid": v(220.16, -33.28) * mm, "end": v(222.5, -27.62) * mm});
            skLineSegment(sketch, "E348.0.1.35", {"start": v(222.5, -25) * mm, "end": v(222.5, -27.62) * mm});
            skArc(sketch, "E348.0.1.36", {"start": v(181, -72) * mm, "mid": v(190.65, -47.27) * mm, "end": v(214.5, -35.62) * mm});
            skArc(sketch, "E348.0.1.37", {"start": v(190.5, -72) * mm, "mid": v(197.03, -54.4) * mm, "end": v(213.46, -45.3) * mm});
            skArc(sketch, "E348.0.1.38", {"start": v(195.5, -72) * mm, "mid": v(197.99, -61.84) * mm, "end": v(204.88, -53.98) * mm});
            skArc(sketch, "E348.0.1.39", {"start": v(214.5, -58.76) * mm, "mid": v(211.17, -53.4) * mm, "end": v(204.88, -53.98) * mm});
            skArc(sketch, "E348.0.1.40", {"start": v(222.5, -53.24) * mm, "mid": v(219.78, -47.22) * mm, "end": v(213.46, -45.3) * mm});
            skLineSegment(sketch, "E348.0.1.41", {"start": v(214.5, -58.76) * mm, "end": v(214.58, -259.5) * mm});
            skLineSegment(sketch, "E348.0.1.42", {"start": v(222.5, -280) * mm, "end": v(222.5, -53.24) * mm});
            skArc(sketch, "E348.0.1.43", {"start": v(202.08, -272) * mm, "mid": v(210.92, -268.34) * mm, "end": v(214.58, -259.5) * mm});
            skLineSegment(sketch, "E348.0.2.0", {"start": v(7.5, -10) * mm, "end": v(7.5, 245) * mm});
            skLineSegment(sketch, "E348.0.2.1", {"start": v(7.5, 245) * mm, "end": v(222.5, 245) * mm});
            skArc(sketch, "E348.0.2.2", {"start": v(23.5, 237) * mm, "mid": v(19.26, 235.24) * mm, "end": v(17.5, 231) * mm});
            skLineSegment(sketch, "E348.0.2.3", {"start": v(66.98, 237) * mm, "end": v(23.5, 237) * mm});
            skLineSegment(sketch, "E348.0.2.4", {"start": v(17.5, 231) * mm, "end": v(17.5, 139.3) * mm});
            skLineSegment(sketch, "E348.0.2.5", {"start": v(72.98, 231) * mm, "end": v(72.98, 153.5) * mm});
            skLineSegment(sketch, "E348.0.2.6", {"start": v(78.98, 231) * mm, "end": v(78.98, 151) * mm});
            skArc(sketch, "E348.0.2.7", {"start": v(72.98, 231) * mm, "mid": v(71.22, 235.24) * mm, "end": v(66.98, 237) * mm});
            skArc(sketch, "E348.0.2.8", {"start": v(84.98, 237) * mm, "mid": v(80.74, 235.24) * mm, "end": v(78.98, 231) * mm});
            skLineSegment(sketch, "E348.0.2.9", {"start": v(84.98, 237) * mm, "end": v(182.84, 237) * mm});
            skArc(sketch, "E348.0.2.10", {"start": v(17.5, 139.3) * mm, "mid": v(19.26, 135.05) * mm, "end": v(23.5, 133.3) * mm});
            skArc(sketch, "E348.0.2.11", {"start": v(23.5, 127.3) * mm, "mid": v(17.84, 124.95) * mm, "end": v(15.5, 119.3) * mm});
            skArc(sketch, "E348.0.2.12", {"start": v(23.5, 133.3) * mm, "mid": v(48.17, 138.25) * mm, "end": v(70.92, 148.98) * mm});
            skArc(sketch, "E348.0.2.13", {"start": v(23.5, 127.3) * mm, "mid": v(51.54, 133.07) * mm, "end": v(77.13, 145.89) * mm});
            skArc(sketch, "E348.0.2.14", {"start": v(70.92, 148.98) * mm, "mid": v(72.44, 151.02) * mm, "end": v(72.98, 153.5) * mm});
            skArc(sketch, "E348.0.2.15", {"start": v(77.13, 145.89) * mm, "mid": v(78.5, 148.28) * mm, "end": v(78.98, 151) * mm});
            skLineSegment(sketch, "E348.0.2.16", {"start": v(15.5, 119.3) * mm, "end": v(15.5, 10.5) * mm});
            skArc(sketch, "E348.0.2.17", {"start": v(28, -2) * mm, "mid": v(19.16, 1.66) * mm, "end": v(15.5, 10.5) * mm});
            skLineSegment(sketch, "E348.0.2.18", {"start": v(7.5, -10) * mm, "end": v(222.5, -10) * mm});
            skLineSegment(sketch, "E348.0.2.19", {"start": v(28, -2) * mm, "end": v(202.08, -2) * mm});
            skArc(sketch, "E348.0.2.20", {"start": v(195.5, 92) * mm, "mid": v(135.83, 14.24) * mm, "end": v(45.28, 51.75) * mm});
            skArc(sketch, "E348.0.2.21", {"start": v(190.5, 92) * mm, "mid": v(134.54, 19.07) * mm, "end": v(49.62, 54.25) * mm});
            skArc(sketch, "E348.0.2.22", {"start": v(181, 92) * mm, "mid": v(132.08, 28.25) * mm, "end": v(57.84, 59) * mm});
            skArc(sketch, "E348.0.2.23", {"start": v(176, 92) * mm, "mid": v(130.79, 33.08) * mm, "end": v(62.17, 61.5) * mm});
            skArc(sketch, "E348.0.2.24", {"start": v(62.17, 61.5) * mm, "mid": v(58.76, 62.42) * mm, "end": v(57.84, 59) * mm});
            skArc(sketch, "E348.0.2.25", {"start": v(49.62, 54.25) * mm, "mid": v(46.2, 55.17) * mm, "end": v(45.28, 51.75) * mm});
            skLineSegment(sketch, "E348.0.2.26", {"start": v(115, 92) * mm, "end": v(28.4, 42) * mm, "construction": true});
            skPoint(sketch, "E348.0.2.27", {"position": v(115, 117.5) * mm});
            skLineSegment(sketch, "E348.0.2.28", {"start": v(176, 92) * mm, "end": v(176, 198) * mm});
            skLineSegment(sketch, "E348.0.2.29", {"start": v(181, 92) * mm, "end": v(181, 198) * mm});
            skLineSegment(sketch, "E348.0.2.30", {"start": v(190.5, 92) * mm, "end": v(190.5, 198) * mm});
            skLineSegment(sketch, "E348.0.2.31", {"start": v(195.5, 92) * mm, "end": v(195.5, 198) * mm});
            skArc(sketch, "E348.0.2.32", {"start": v(176, 198) * mm, "mid": v(179, 214.15) * mm, "end": v(187.98, 227.9) * mm});
            skArc(sketch, "E348.0.2.33", {"start": v(187.98, 227.9) * mm, "mid": v(188.07, 233.95) * mm, "end": v(182.84, 237) * mm});
            skArc(sketch, "E348.0.2.34", {"start": v(214.5, 234.38) * mm, "mid": v(220.16, 236.72) * mm, "end": v(222.5, 242.38) * mm});
            skLineSegment(sketch, "E348.0.2.35", {"start": v(222.5, 245) * mm, "end": v(222.5, 242.38) * mm});
            skArc(sketch, "E348.0.2.36", {"start": v(181, 198) * mm, "mid": v(190.65, 222.73) * mm, "end": v(214.5, 234.38) * mm});
            skArc(sketch, "E348.0.2.37", {"start": v(190.5, 198) * mm, "mid": v(197.03, 215.6) * mm, "end": v(213.46, 224.7) * mm});
            skArc(sketch, "E348.0.2.38", {"start": v(195.5, 198) * mm, "mid": v(197.99, 208.16) * mm, "end": v(204.88, 216.02) * mm});
            skArc(sketch, "E348.0.2.39", {"start": v(214.5, 211.24) * mm, "mid": v(211.17, 216.6) * mm, "end": v(204.88, 216.02) * mm});
            skArc(sketch, "E348.0.2.40", {"start": v(222.5, 216.76) * mm, "mid": v(219.78, 222.78) * mm, "end": v(213.46, 224.7) * mm});
            skLineSegment(sketch, "E348.0.2.41", {"start": v(214.5, 211.24) * mm, "end": v(214.58, 10.5) * mm});
            skLineSegment(sketch, "E348.0.2.42", {"start": v(222.5, -10) * mm, "end": v(222.5, 216.76) * mm});
            skArc(sketch, "E348.0.2.43", {"start": v(202.08, -2) * mm, "mid": v(210.92, 1.66) * mm, "end": v(214.58, 10.5) * mm});
            skLineSegment(sketch, "E348.0.3.0", {"start": v(7.5, 260) * mm, "end": v(7.5, 515) * mm});
            skLineSegment(sketch, "E348.0.3.1", {"start": v(7.5, 515) * mm, "end": v(222.5, 515) * mm});
            skArc(sketch, "E348.0.3.2", {"start": v(23.5, 507) * mm, "mid": v(19.26, 505.24) * mm, "end": v(17.5, 501) * mm});
            skLineSegment(sketch, "E348.0.3.3", {"start": v(66.98, 507) * mm, "end": v(23.5, 507) * mm});
            skLineSegment(sketch, "E348.0.3.4", {"start": v(17.5, 501) * mm, "end": v(17.5, 409.3) * mm});
            skLineSegment(sketch, "E348.0.3.5", {"start": v(72.98, 501) * mm, "end": v(72.98, 423.5) * mm});
            skLineSegment(sketch, "E348.0.3.6", {"start": v(78.98, 501) * mm, "end": v(78.98, 421) * mm});
            skArc(sketch, "E348.0.3.7", {"start": v(72.98, 501) * mm, "mid": v(71.22, 505.24) * mm, "end": v(66.98, 507) * mm});
            skArc(sketch, "E348.0.3.8", {"start": v(84.98, 507) * mm, "mid": v(80.74, 505.24) * mm, "end": v(78.98, 501) * mm});
            skLineSegment(sketch, "E348.0.3.9", {"start": v(84.98, 507) * mm, "end": v(182.84, 507) * mm});
            skArc(sketch, "E348.0.3.10", {"start": v(17.5, 409.3) * mm, "mid": v(19.26, 405.05) * mm, "end": v(23.5, 403.3) * mm});
            skArc(sketch, "E348.0.3.11", {"start": v(23.5, 397.3) * mm, "mid": v(17.84, 394.95) * mm, "end": v(15.5, 389.3) * mm});
            skArc(sketch, "E348.0.3.12", {"start": v(23.5, 403.3) * mm, "mid": v(48.17, 408.25) * mm, "end": v(70.92, 418.98) * mm});
            skArc(sketch, "E348.0.3.13", {"start": v(23.5, 397.3) * mm, "mid": v(51.54, 403.07) * mm, "end": v(77.13, 415.89) * mm});
            skArc(sketch, "E348.0.3.14", {"start": v(70.92, 418.98) * mm, "mid": v(72.44, 421.02) * mm, "end": v(72.98, 423.5) * mm});
            skArc(sketch, "E348.0.3.15", {"start": v(77.13, 415.89) * mm, "mid": v(78.5, 418.28) * mm, "end": v(78.98, 421) * mm});
            skLineSegment(sketch, "E348.0.3.16", {"start": v(15.5, 389.3) * mm, "end": v(15.5, 280.5) * mm});
            skArc(sketch, "E348.0.3.17", {"start": v(28, 268) * mm, "mid": v(19.16, 271.66) * mm, "end": v(15.5, 280.5) * mm});
            skLineSegment(sketch, "E348.0.3.18", {"start": v(7.5, 260) * mm, "end": v(222.5, 260) * mm});
            skLineSegment(sketch, "E348.0.3.19", {"start": v(28, 268) * mm, "end": v(202.08, 268) * mm});
            skArc(sketch, "E348.0.3.20", {"start": v(195.5, 362) * mm, "mid": v(135.83, 284.24) * mm, "end": v(45.28, 321.75) * mm});
            skArc(sketch, "E348.0.3.21", {"start": v(190.5, 362) * mm, "mid": v(134.54, 289.07) * mm, "end": v(49.62, 324.25) * mm});
            skArc(sketch, "E348.0.3.22", {"start": v(181, 362) * mm, "mid": v(132.08, 298.25) * mm, "end": v(57.84, 329) * mm});
            skArc(sketch, "E348.0.3.23", {"start": v(176, 362) * mm, "mid": v(130.79, 303.08) * mm, "end": v(62.17, 331.5) * mm});
            skArc(sketch, "E348.0.3.24", {"start": v(62.17, 331.5) * mm, "mid": v(58.76, 332.42) * mm, "end": v(57.84, 329) * mm});
            skArc(sketch, "E348.0.3.25", {"start": v(49.62, 324.25) * mm, "mid": v(46.2, 325.17) * mm, "end": v(45.28, 321.75) * mm});
            skLineSegment(sketch, "E348.0.3.26", {"start": v(115, 362) * mm, "end": v(28.4, 312) * mm, "construction": true});
            skPoint(sketch, "E348.0.3.27", {"position": v(115, 387.5) * mm});
            skLineSegment(sketch, "E348.0.3.28", {"start": v(176, 362) * mm, "end": v(176, 468) * mm});
            skLineSegment(sketch, "E348.0.3.29", {"start": v(181, 362) * mm, "end": v(181, 468) * mm});
            skLineSegment(sketch, "E348.0.3.30", {"start": v(190.5, 362) * mm, "end": v(190.5, 468) * mm});
            skLineSegment(sketch, "E348.0.3.31", {"start": v(195.5, 362) * mm, "end": v(195.5, 468) * mm});
            skArc(sketch, "E348.0.3.32", {"start": v(176, 468) * mm, "mid": v(179, 484.15) * mm, "end": v(187.98, 497.9) * mm});
            skArc(sketch, "E348.0.3.33", {"start": v(187.98, 497.9) * mm, "mid": v(188.07, 503.95) * mm, "end": v(182.84, 507) * mm});
            skArc(sketch, "E348.0.3.34", {"start": v(214.5, 504.38) * mm, "mid": v(220.16, 506.72) * mm, "end": v(222.5, 512.38) * mm});
            skLineSegment(sketch, "E348.0.3.35", {"start": v(222.5, 515) * mm, "end": v(222.5, 512.38) * mm});
            skArc(sketch, "E348.0.3.36", {"start": v(181, 468) * mm, "mid": v(190.65, 492.73) * mm, "end": v(214.5, 504.38) * mm});
            skArc(sketch, "E348.0.3.37", {"start": v(190.5, 468) * mm, "mid": v(197.03, 485.6) * mm, "end": v(213.46, 494.7) * mm});
            skArc(sketch, "E348.0.3.38", {"start": v(195.5, 468) * mm, "mid": v(197.99, 478.16) * mm, "end": v(204.88, 486.02) * mm});
            skArc(sketch, "E348.0.3.39", {"start": v(214.5, 481.24) * mm, "mid": v(211.17, 486.6) * mm, "end": v(204.88, 486.02) * mm});
            skArc(sketch, "E348.0.3.40", {"start": v(222.5, 486.76) * mm, "mid": v(219.78, 492.78) * mm, "end": v(213.46, 494.7) * mm});
            skLineSegment(sketch, "E348.0.3.41", {"start": v(214.5, 481.24) * mm, "end": v(214.58, 280.5) * mm});
            skLineSegment(sketch, "E348.0.3.42", {"start": v(222.5, 260) * mm, "end": v(222.5, 486.76) * mm});
            skArc(sketch, "E348.0.3.43", {"start": v(202.08, 268) * mm, "mid": v(210.92, 271.66) * mm, "end": v(214.58, 280.5) * mm});
            skLineSegment(sketch, "E348.direction1", {"start": v(7.5, -550) * mm, "end": v(32.5, -550) * mm, "construction": true});
            skLineSegment(sketch, "E348.direction2", {"start": v(7.5, -550) * mm, "end": v(7.5, -280) * mm, "construction": true});
            skSolve(sketch);
        }
        {
            var Q0;
            Q0 = qSketchRegion(id + "F4", true);
            extrude(context, id + "F5", {"entities" : qUnion([Q0]), "depth" : 24 * mm, "offsetDistance" : 25 * mm});
        }
    });
